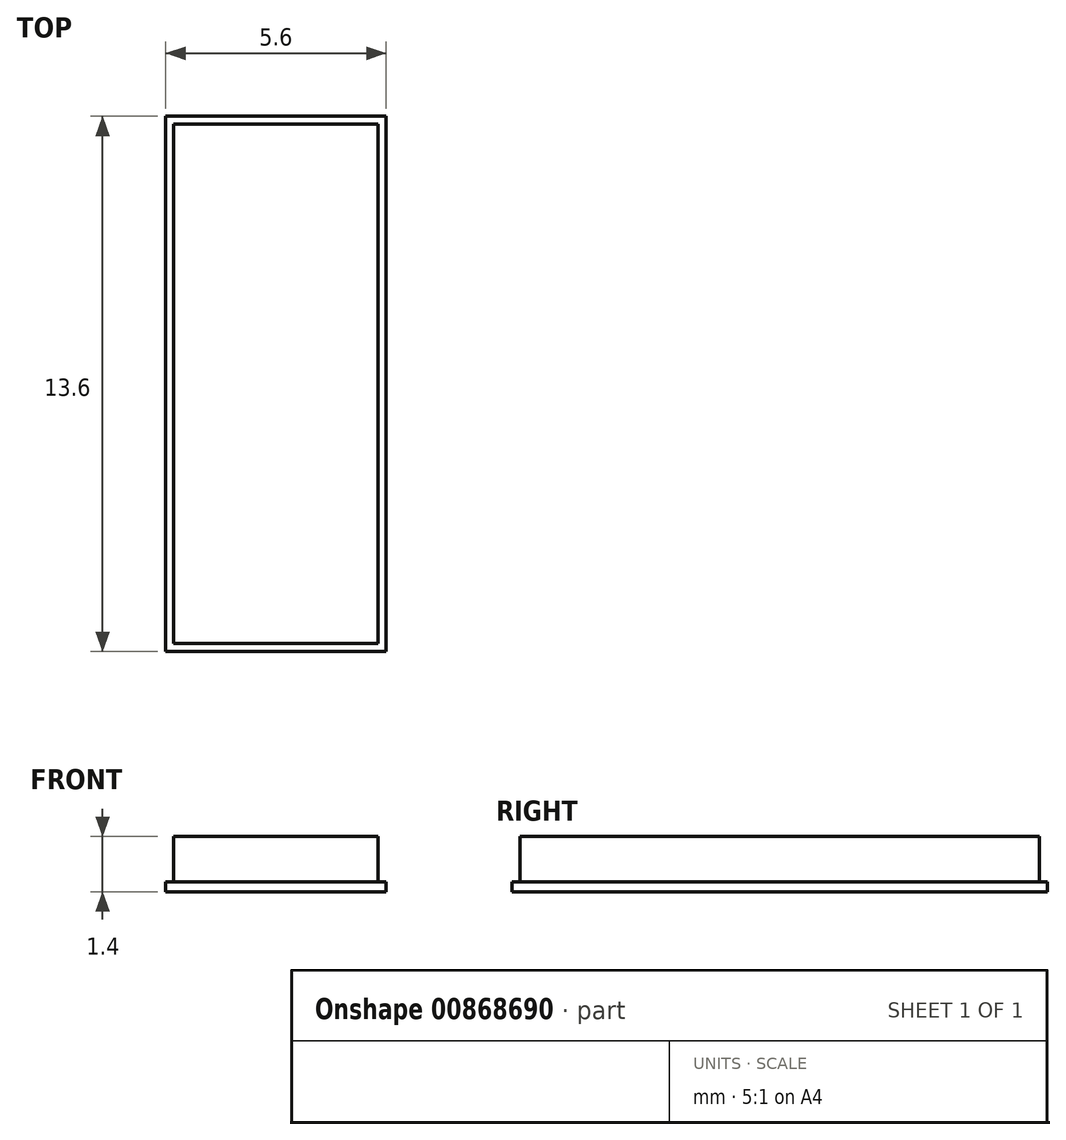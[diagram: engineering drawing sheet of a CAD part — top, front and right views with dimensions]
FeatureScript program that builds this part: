
annotation { "Feature Type Name" : "Feature", "Feature Type Description" : "" }
export const myFeature = defineFeature(function(context is Context, id is Id, definition is map)
    precondition{}
    {
        {
            var Q0;
            Q0=qCreatedBy(makeId("Top.planeOp"),FACE);
            var sketch = newSketch(context, id + "F0", { "sketchPlane" : qUnion([Q0])});
            skLineSegment(sketch, "E0.bottom", {"start": v(2.8, 6.8) * mm, "end": v(-2.8, 6.8) * mm});
            skLineSegment(sketch, "E0.top", {"start": v(2.8, -6.8) * mm, "end": v(-2.8, -6.8) * mm});
            skLineSegment(sketch, "E0.left", {"start": v(2.8, 6.8) * mm, "end": v(2.8, -6.8) * mm});
            skLineSegment(sketch, "E0.right", {"start": v(-2.8, 6.8) * mm, "end": v(-2.8, -6.8) * mm});
            skPoint(sketch, "E0.middle", {"position": v(0, 0) * mm});
            skLineSegment(sketch, "E1.bottom", {"start": v(-2.6, 6.6) * mm, "end": v(2.6, 6.6) * mm});
            skLineSegment(sketch, "E1.top", {"start": v(-2.6, -6.6) * mm, "end": v(2.6, -6.6) * mm});
            skLineSegment(sketch, "E1.left", {"start": v(-2.6, 6.6) * mm, "end": v(-2.6, -6.6) * mm});
            skLineSegment(sketch, "E1.right", {"start": v(2.6, 6.6) * mm, "end": v(2.6, -6.6) * mm});
            skSolve(sketch);
        }
        {
            var Q0;
            Q0=makeQuery(id+"F0.imprint","IMPRINT",FACE,{"disambiguationData":[TD([[makeQuery(id+"F0.imprint","IMPRINT",EDGE,{"derivedFrom":sQuery(id+"F0.wireOp",EDGE,"E1.bottom")}),-1.0]])]});
            extrude(context, id + "F1", {"entities" : qUnion([Q0]), "depth" : 1.4 * mm, "offsetDistance" : 25.4 * mm});
        }
        {
            var Q0;
            Q0 = qSketchRegion(id + "F0", true);
            extrude(context, id + "F2", {"entities" : qUnion([Q0]), "operationType" : NewBodyOperationType.ADD, "depth" : .25 * mm, "offsetDistance" : 25.4 * mm});
        }
    });
